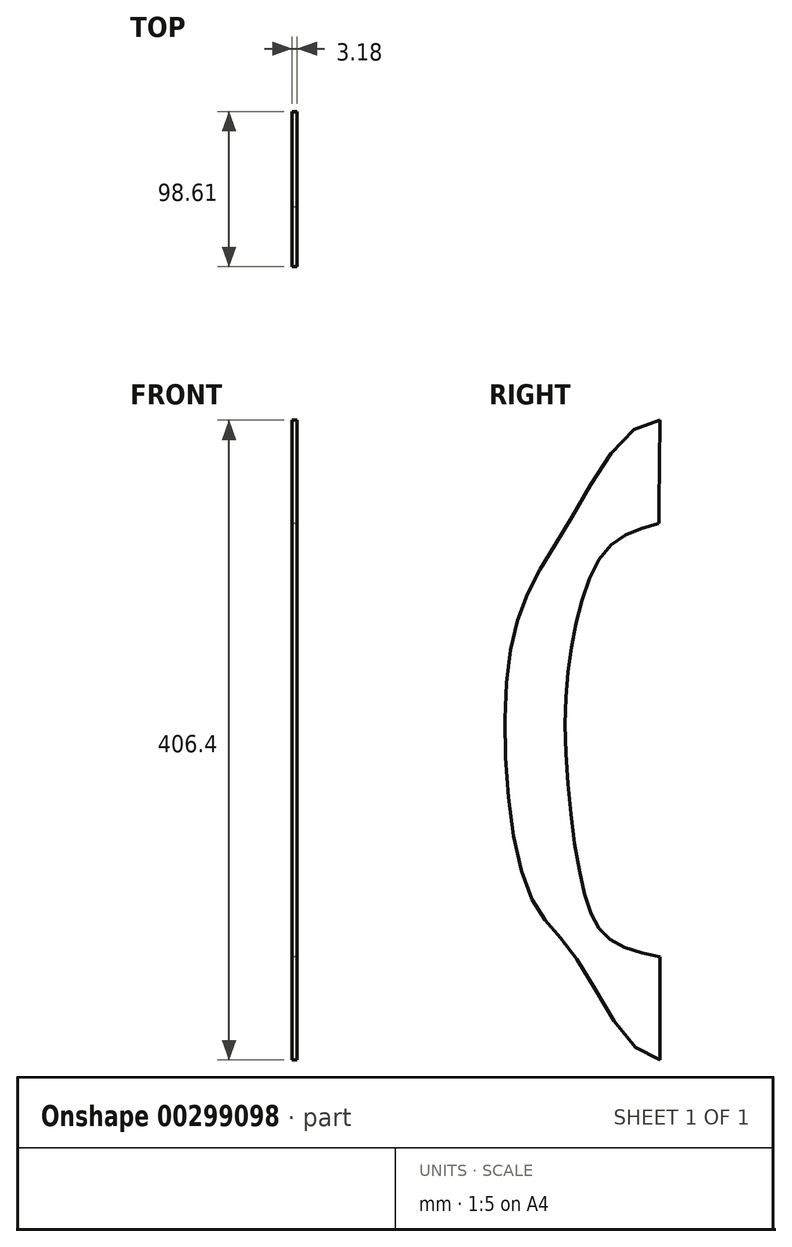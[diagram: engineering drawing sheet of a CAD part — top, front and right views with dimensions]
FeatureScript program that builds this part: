
annotation { "Feature Type Name" : "Feature", "Feature Type Description" : "" }
export const myFeature = defineFeature(function(context is Context, id is Id, definition is map)
    precondition{}
    {
        {
            var Q0;
            Q0=qCreatedBy(makeId("Right.planeOp"),FACE);
            var sketch = newSketch(context, id + "F0", { "sketchPlane" : qUnion([Q0])});
            skLineSegment(sketch, "E0", {"start": v(0, 0) * mm, "end": v(0, 203.2) * mm, "construction": true});
            skLineSegment(sketch, "E1", {"start": v(0, 0) * mm, "end": v(0, -203.2) * mm, "construction": true});
            skFitSpline(sketch, "E2", {"points": [v(0, 203.2) * mm, v(-55.82, 142.1) * mm, v(-87.85, 84.26) * mm, v(-98.52, 0) * mm, v(-81.62, -100.8) * mm, v(-52.26, -139.95) * mm, v(0, -203.2) * mm], "startDerivative": vector(-402.38, 0.49) * mm, "endDerivative": vector(385.16, -45.32) * mm});
            skFitSpline(sketch, "E3", {"points": [v(-0.91, 137.63) * mm, v(0, 203.2) * mm], "startDerivative": vector(0.91, 14.77) * mm, "endDerivative": vector(0.91, 14.77) * mm});
            skFitSpline(sketch, "E4", {"points": [v(-0.91, 137.63) * mm, v(-32.2, 123.1) * mm, v(-53.38, 74.48) * mm, v(-60.13, 0) * mm, v(-49, -93.29) * mm, v(-32.78, -125.74) * mm, v(0, -137.73) * mm], "startDerivative": vector(-252.12, -67.35) * mm, "endDerivative": vector(270.73, -60.66) * mm});
            skFitSpline(sketch, "E5", {"points": [v(0, -137.73) * mm, v(0, -203.2) * mm], "startDerivative": vector(0, -65.47) * mm, "endDerivative": vector(0, -65.47) * mm});
            skSolve(sketch);
        }
        {
            var Q0;
            Q0 = qSketchRegion(id + "F0", true);
            extrude(context, id + "F1", {"entities" : qUnion([Q0]), "depth" : 3.17 * mm});
        }
    });
